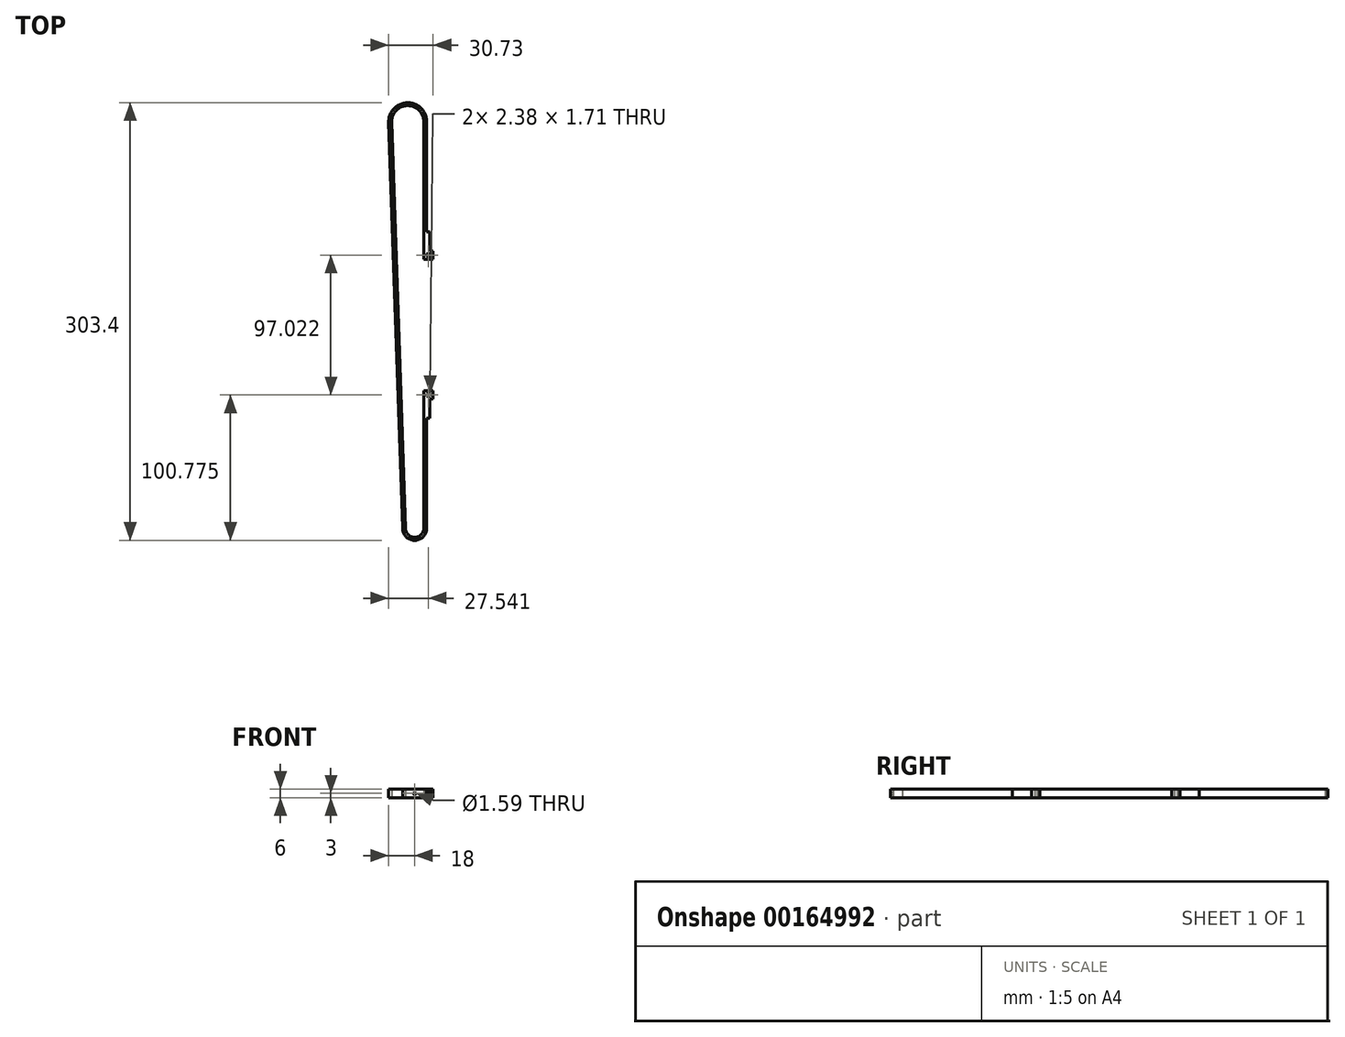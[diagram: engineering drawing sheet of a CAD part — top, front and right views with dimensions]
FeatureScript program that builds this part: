
annotation { "Feature Type Name" : "Feature", "Feature Type Description" : "" }
export const myFeature = defineFeature(function(context is Context, id is Id, definition is map)
    precondition{}
    {
        {
            var Q0;
            Q0=qCreatedBy(makeId("Top.planeOp"),FACE);
            var sketch = newSketch(context, id + "F0", { "sketchPlane" : qUnion([Q0])});
            skLineSegment(sketch, "E0.bottom", {"start": v(0, 0) * mm, "end": v(2.38, 0) * mm});
            skLineSegment(sketch, "E0.top", {"start": v(0, -1.7) * mm, "end": v(2.38, -1.7) * mm});
            skLineSegment(sketch, "E0.left", {"start": v(0, 0) * mm, "end": v(0, -1.7) * mm});
            skLineSegment(sketch, "E0.right", {"start": v(2.38, 0) * mm, "end": v(2.38, -1.7) * mm});
            skLineSegment(sketch, "E1", {"start": v(0, -0.85) * mm, "end": v(-2, -0.85) * mm, "construction": true});
            skLineSegment(sketch, "E2", {"start": v(2.38, -0.85) * mm, "end": v(4.38, -0.85) * mm, "construction": true});
            skLineSegment(sketch, "E3", {"start": v(1.2, 0) * mm, "end": v(1.2, 2) * mm, "construction": true});
            skLineSegment(sketch, "E4", {"start": v(1.2, -1.7) * mm, "end": v(1.2, -3.7) * mm, "construction": true});
            skLineSegment(sketch, "E5.top", {"start": v(-2, 2) * mm, "end": v(4.38, 2) * mm});
            skLineSegment(sketch, "E5.left", {"start": v(-2, -93.28) * mm, "end": v(-2, 2) * mm});
            skLineSegment(sketch, "E5.right", {"start": v(4.38, -3.7) * mm, "end": v(4.38, 2) * mm});
            skLineSegment(sketch, "E6", {"start": v(-2, -93.28) * mm, "end": v(0, -93.28) * mm, "construction": true});
            skLineSegment(sketch, "E7", {"start": v(-2, -93.28) * mm, "end": v(-14.7, -93.28) * mm, "construction": true});
            skLineSegment(sketch, "E8", {"start": v(-14.7, -93.28) * mm, "end": v(-16.7, -93.28) * mm, "construction": true});
            skArc(sketch, "E9", {"start": v(-14.7, -93.28) * mm, "mid": v(-8.35, -99.63) * mm, "end": v(-2, -93.28) * mm});
            skArc(sketch, "E10", {"start": v(-16.7, -93.28) * mm, "mid": v(-8.35, -101.63) * mm, "end": v(0, -93.28) * mm});
            skLineSegment(sketch, "E11", {"start": v(0, -93.28) * mm, "end": v(0, -17.08) * mm});
            skLineSegment(sketch, "E12", {"start": v(4.38, -3.7) * mm, "end": v(2, -3.7) * mm});
            skLineSegment(sketch, "E13", {"start": v(2, -3.7) * mm, "end": v(2, -17.08) * mm});
            skLineSegment(sketch, "E14", {"start": v(2, -17.08) * mm, "end": v(0, -17.08) * mm});
            skLineSegment(sketch, "E15", {"start": v(1.2, -3.7) * mm, "end": v(2, -3.7) * mm});
            skLineSegment(sketch, "E16", {"start": v(1.2, 2) * mm, "end": v(1.2, 93.31) * mm, "construction": true});
            skLineSegment(sketch, "E17", {"start": v(1.2, 93.31) * mm, "end": v(1.2, 95.31) * mm, "construction": true});
            skLineSegment(sketch, "E18.bottom", {"start": v(2.38, 97.02) * mm, "end": v(0, 97.02) * mm});
            skLineSegment(sketch, "E18.top", {"start": v(2.38, 95.31) * mm, "end": v(0, 95.31) * mm});
            skLineSegment(sketch, "E18.left", {"start": v(2.38, 97.02) * mm, "end": v(2.38, 95.31) * mm});
            skLineSegment(sketch, "E18.right", {"start": v(0, 97.02) * mm, "end": v(0, 95.31) * mm});
            skLineSegment(sketch, "E19", {"start": v(0, 96.17) * mm, "end": v(-2, 96.17) * mm, "construction": true});
            skLineSegment(sketch, "E20", {"start": v(2.38, 96.17) * mm, "end": v(4.38, 96.17) * mm, "construction": true});
            skLineSegment(sketch, "E21", {"start": v(1.2, 97.02) * mm, "end": v(1.2, 99.02) * mm, "construction": true});
            skLineSegment(sketch, "E22", {"start": v(4.38, 93.31) * mm, "end": v(-2, 93.31) * mm});
            skLineSegment(sketch, "E23", {"start": v(-2, 93.31) * mm, "end": v(-2, 188.6) * mm});
            skLineSegment(sketch, "E24", {"start": v(4.38, 93.31) * mm, "end": v(4.38, 99.02) * mm});
            skLineSegment(sketch, "E25", {"start": v(4.38, 99.02) * mm, "end": v(2, 99.02) * mm});
            skLineSegment(sketch, "E26", {"start": v(2, 99.02) * mm, "end": v(2, 112.4) * mm});
            skLineSegment(sketch, "E27", {"start": v(2, 112.4) * mm, "end": v(0, 112.4) * mm});
            skLineSegment(sketch, "E28", {"start": v(0, 112.4) * mm, "end": v(0, 188.6) * mm});
            skLineSegment(sketch, "E29", {"start": v(-2, 188.6) * mm, "end": v(0, 188.6) * mm, "construction": true});
            skLineSegment(sketch, "E30", {"start": v(-24.34, 188.14) * mm, "end": v(-26.34, 188.14) * mm, "construction": true});
            skArc(sketch, "E31", {"start": v(-2, 188.6) * mm, "mid": v(-13.4, 199.77) * mm, "end": v(-24.34, 188.14) * mm});
            skArc(sketch, "E32", {"start": v(0, 188.6) * mm, "mid": v(-13.4, 201.77) * mm, "end": v(-26.34, 188.14) * mm});
            skLineSegment(sketch, "E33", {"start": v(-14.7, -93.28) * mm, "end": v(-24.34, 188.14) * mm});
            skLineSegment(sketch, "E34", {"start": v(-26.34, 188.14) * mm, "end": v(-16.7, -93.28) * mm});
            skLineSegment(sketch, "E35", {"start": v(1.2, 99.02) * mm, "end": v(2, 99.02) * mm, "construction": true});
            skLineSegment(sketch, "E36", {"start": v(-8.35, -93.28) * mm, "end": v(-8.35, 188.6) * mm, "construction": true});
            skLineSegment(sketch, "E37", {"start": v(-8.35, 188.6) * mm, "end": v(-13.17, 188.6) * mm, "construction": true});
            skSolve(sketch);
        }
        {
            var Q0;
            Q0=qSketchRegion(id+"F0",true);
            extrude(context, id + "F1", {"entities" : qUnion([Q0]), "depth" : 6 * mm});
        }
        {
            var Q0;
            Q0=makeQuery(id+"F1.opExtrude","SWEPT_FACE",FACE,{"disambiguationData":[OSD([sQuery(id+"F0.wireOp",EDGE,"E5.top")])]});
            var sketch = newSketch(context, id + "F2", { "sketchPlane" : qUnion([Q0])});
            skLineSegment(sketch, "E38", {"start": v(2, 3) * mm, "end": v(8.35, 3) * mm, "construction": true});
            skLineSegment(sketch, "E39", {"start": v(8.35, 3) * mm, "end": v(8.35, 6) * mm, "construction": true});
            skCircle(sketch, "E40", {"center": v(8.35, 3) * mm, "radius": 0.8 * mm});
            skSolve(sketch);
        }
        {
            var Q0;
            Q0 = qSketchRegion(id + "F2", true);
            var Q1;
            Q1=makeQuery(id+"F1.opExtrude","SWEPT_FACE",FACE,{"disambiguationData":[OSD([sQuery(id+"F0.wireOp",EDGE,"E10")])]});
            extrude(context, id + "F3", {"entities" : qUnion([Q0]), "operationType" : NewBodyOperationType.REMOVE, "endBound" : BoundingType.THROUGH_ALL, "oppositeDirection" : true, "endBoundEntityFace" : qUnion([Q1]), "depth" : 25.4 * mm});
        }
    });
